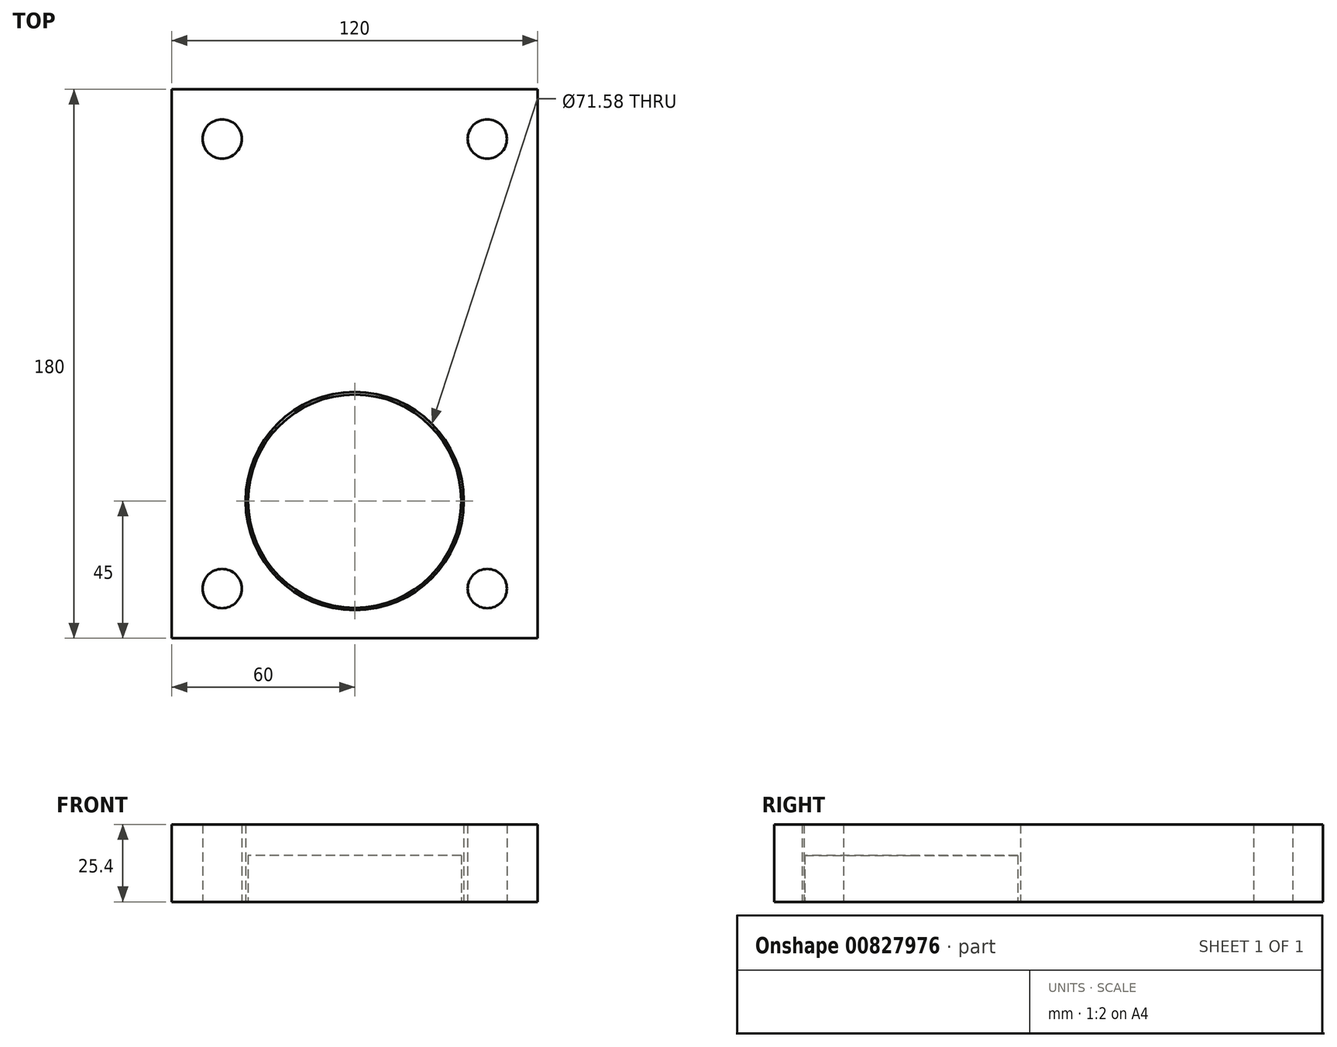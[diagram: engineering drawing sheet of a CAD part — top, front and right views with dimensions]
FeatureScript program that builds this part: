
annotation { "Feature Type Name" : "Feature", "Feature Type Description" : "" }
export const myFeature = defineFeature(function(context is Context, id is Id, definition is map)
    precondition{}
    {
        {
            var Q0;
            Q0=qCreatedBy(makeId("Top.planeOp"),FACE);
            var sketch = newSketch(context, id + "F0", { "sketchPlane" : qUnion([Q0])});
            skLineSegment(sketch, "E0.bottom", {"start": v(-60, 90) * mm, "end": v(60, 90) * mm});
            skLineSegment(sketch, "E0.top", {"start": v(-60, -90) * mm, "end": v(60, -90) * mm});
            skLineSegment(sketch, "E0.left", {"start": v(-60, 90) * mm, "end": v(-60, -90) * mm});
            skLineSegment(sketch, "E0.right", {"start": v(60, 90) * mm, "end": v(60, -90) * mm});
            skPoint(sketch, "E0.middle", {"position": v(0, 0) * mm});
            skCircle(sketch, "E1", {"center": v(0, -45) * mm, "radius": 35.79 * mm});
            skLineSegment(sketch, "E2.bottom", {"start": v(-43.48, 73.7) * mm, "end": v(43.48, 73.7) * mm});
            skLineSegment(sketch, "E2.top", {"start": v(-43.48, -73.7) * mm, "end": v(43.48, -73.7) * mm});
            skLineSegment(sketch, "E2.left", {"start": v(-43.48, 73.7) * mm, "end": v(-43.48, -73.7) * mm});
            skLineSegment(sketch, "E2.right", {"start": v(43.48, 73.7) * mm, "end": v(43.48, -73.7) * mm});
            skCircle(sketch, "E3", {"center": v(-43.48, 73.7) * mm, "radius": 6.44 * mm});
            skLineSegment(sketch, "E4", {"start": v(0, 73.7) * mm, "end": v(0, -73.7) * mm, "construction": true});
            skCircle(sketch, "E5.MirrorC", {"center": v(43.48, 73.7) * mm, "radius": 6.44 * mm});
            skLineSegment(sketch, "E6", {"start": v(-43.48, 0) * mm, "end": v(43.48, 0) * mm});
            skCircle(sketch, "E7.MirrorC", {"center": v(-43.48, -73.7) * mm, "radius": 6.44 * mm});
            skCircle(sketch, "E8.MirrorC", {"center": v(43.48, -73.7) * mm, "radius": 6.44 * mm});
            skSolve(sketch);
        }
        {
            var Q0;
            Q0 = qSketchRegion(id + "F0", true);
            var Q1;
            {var subQ5=sQuery(id+"F0.wireOp",EDGE,"E6");Q1=makeQuery(id+"F0.imprint","IMPRINT",FACE,{"disambiguationData":[TD([[makeQuery(id+"F0.imprint","IMPRINT",EDGE,{"derivedFrom":subQ5}),1.0]])]});}
            var Q2;
            {var subQ0=sQuery(id+"F0.wireOp",EDGE,"E6");Q2=makeQuery(id+"F0.imprint","IMPRINT",FACE,{"disambiguationData":[TD([[makeQuery(id+"F0.imprint","IMPRINT",EDGE,{"derivedFrom":subQ0}),-1.0]])]});}
            extrude(context, id + "F1", {"entities" : qUnion([Q0, Q1, Q2]), "depth" : 25.4 * mm, "offsetDistance" : 25.4 * mm});
        }
        {
            var Q0;
            Q0=qCreatedBy(makeId("Top.planeOp"),FACE);
            var sketch = newSketch(context, id + "F2", { "sketchPlane" : qUnion([Q0])});
            skLineSegment(sketch, "E9", {"start": v(0, 0) * mm, "end": v(0, -90.1) * mm, "construction": true});
            skCircle(sketch, "E10", {"center": v(0, -45.05) * mm, "radius": 34.95 * mm});
            skSolve(sketch);
        }
        {
            var Q0;
            Q0 = qSketchRegion(id + "F2", true);
            extrude(context, id + "F3", {"entities" : qUnion([Q0]), "depth" : 15.24 * mm, "offsetDistance" : 25.4 * mm});
        }
    });
